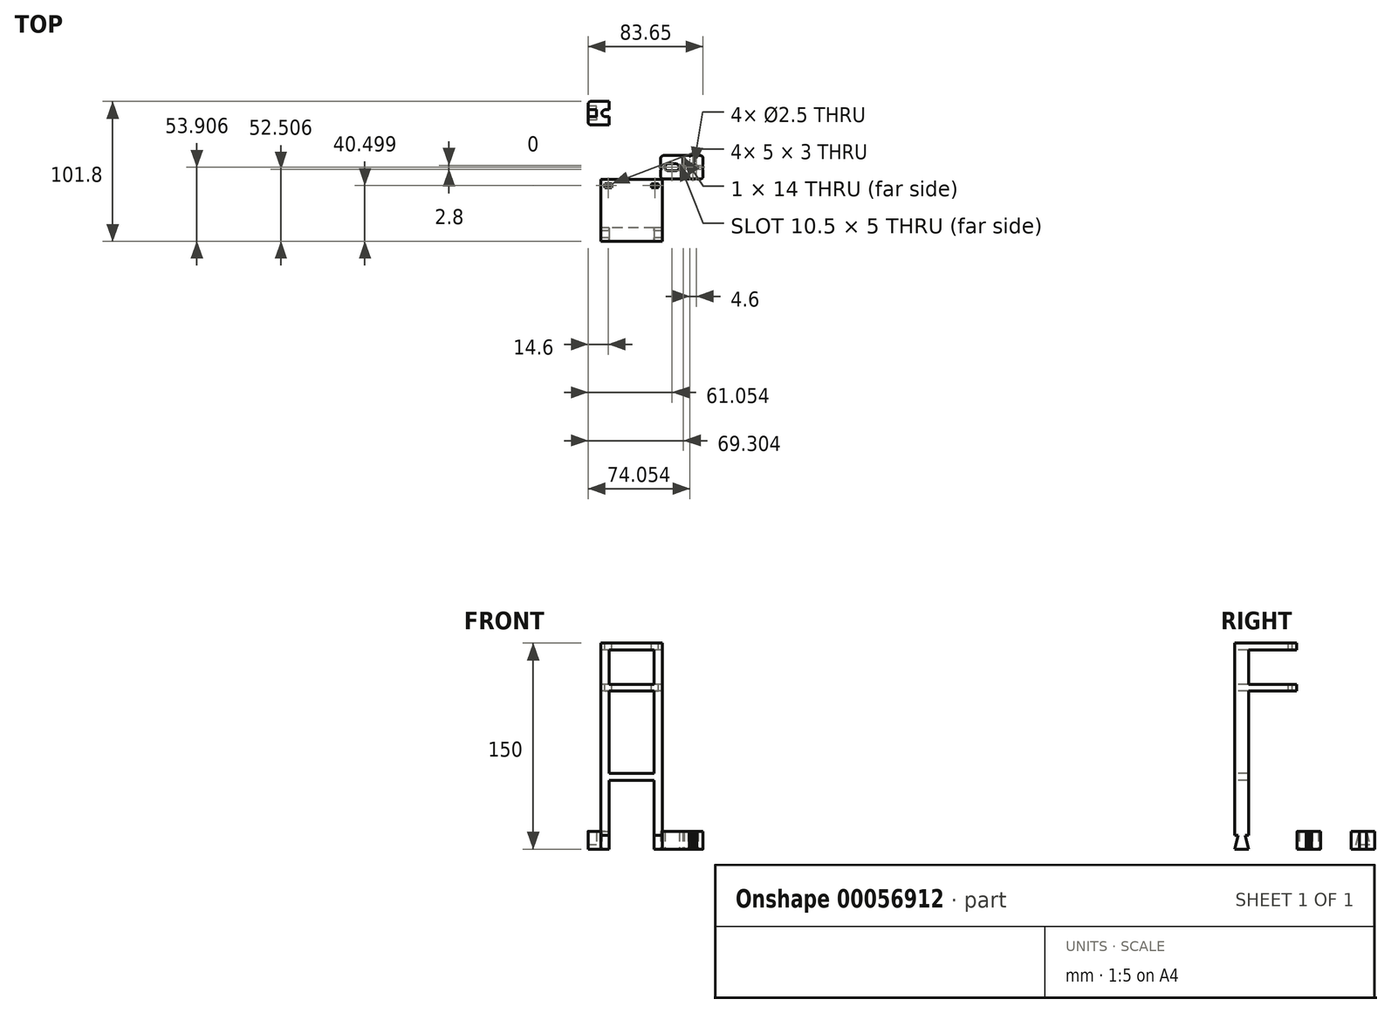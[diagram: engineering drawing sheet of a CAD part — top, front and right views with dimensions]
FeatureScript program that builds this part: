
annotation { "Feature Type Name" : "Feature", "Feature Type Description" : "" }
export const myFeature = defineFeature(function(context is Context, id is Id, definition is map)
    precondition{}
    {
        {
            var Q0;
            Q0=qCreatedBy(makeId("Top.planeOp"),FACE);
            var sketch = newSketch(context, id + "F0", { "sketchPlane" : qUnion([Q0])});
            skLineSegment(sketch, "E0.bottom", {"start": v(1.1, 9.76) * mm, "end": v(19.85, 9.76) * mm});
            skLineSegment(sketch, "E0.top", {"start": v(1.1, -7.24) * mm, "end": v(19.85, -7.24) * mm});
            skLineSegment(sketch, "E0.left", {"start": v(-0.9, 7.76) * mm, "end": v(-0.9, 3.16) * mm});
            skLineSegment(sketch, "E0.right", {"start": v(29.95, 7.76) * mm, "end": v(29.95, 3.16) * mm});
            skCircle(sketch, "E1", {"center": v(20.35, 1.26) * mm, "radius": 1.25 * mm});
            skCircle(sketch, "E2", {"center": v(24.95, 1.26) * mm, "radius": 1.25 * mm});
            skCircle(sketch, "E3", {"center": v(22.65, 2.66) * mm, "radius": 1.25 * mm});
            skCircle(sketch, "E4", {"center": v(22.65, -0.14) * mm, "radius": 1.25 * mm});
            skPoint(sketch, "E5.visualSharp", {"position": v(29.95, 9.76) * mm});
            skArc(sketch, "E5.filletArc", {"start": v(29.95, 7.76) * mm, "mid": v(29.37, 9.17) * mm, "end": v(27.95, 9.76) * mm});
            skPoint(sketch, "E6.visualSharp", {"position": v(29.95, -7.24) * mm});
            skArc(sketch, "E6.filletArc", {"start": v(27.95, -7.24) * mm, "mid": v(29.37, -6.66) * mm, "end": v(29.95, -5.24) * mm});
            skLineSegment(sketch, "E7.bottom", {"start": v(15.1, 8.26) * mm, "end": v(16.1, 8.26) * mm});
            skLineSegment(sketch, "E7.top", {"start": v(15.1, -5.74) * mm, "end": v(16.1, -5.74) * mm});
            skLineSegment(sketch, "E7.left", {"start": v(15.1, 8.26) * mm, "end": v(15.1, -5.74) * mm});
            skLineSegment(sketch, "E7.right", {"start": v(16.1, 8.26) * mm, "end": v(16.1, -5.74) * mm});
            skArc(sketch, "E8", {"start": v(10.1, -1.24) * mm, "mid": v(12.6, 1.26) * mm, "end": v(10.1, 3.76) * mm});
            skPoint(sketch, "E8.centerSnap0", {"position": v(15.1, 1.26) * mm});
            skArc(sketch, "E9", {"start": v(4.6, 3.76) * mm, "mid": v(2.1, 1.26) * mm, "end": v(4.6, -1.24) * mm});
            skLineSegment(sketch, "E10", {"start": v(4.6, 3.76) * mm, "end": v(10.1, 3.76) * mm});
            skLineSegment(sketch, "E11", {"start": v(4.6, -1.24) * mm, "end": v(10.1, -1.24) * mm});
            skPoint(sketch, "E12.visualSharp", {"position": v(-0.9, 9.76) * mm});
            skArc(sketch, "E12.filletArc", {"start": v(1.1, 9.76) * mm, "mid": v(-0.31, 9.17) * mm, "end": v(-0.9, 7.76) * mm});
            skPoint(sketch, "E13.visualSharp", {"position": v(-0.9, -7.24) * mm});
            skArc(sketch, "E13.filletArc", {"start": v(-0.9, -5.24) * mm, "mid": v(-0.31, -6.66) * mm, "end": v(1.1, -7.24) * mm});
            skArc(sketch, "E14", {"start": v(19.85, 9.76) * mm, "mid": v(20.35, 9.26) * mm, "end": v(20.85, 9.76) * mm});
            skArc(sketch, "E15", {"start": v(22.15, 9.76) * mm, "mid": v(22.65, 9.26) * mm, "end": v(23.15, 9.76) * mm});
            skArc(sketch, "E16", {"start": v(24.45, 9.76) * mm, "mid": v(24.95, 9.26) * mm, "end": v(25.45, 9.76) * mm});
            skArc(sketch, "E17", {"start": v(20.85, -7.24) * mm, "mid": v(20.35, -6.74) * mm, "end": v(19.85, -7.24) * mm});
            skArc(sketch, "E18", {"start": v(23.15, -7.24) * mm, "mid": v(22.65, -6.74) * mm, "end": v(22.15, -7.24) * mm});
            skArc(sketch, "E19", {"start": v(25.45, -7.24) * mm, "mid": v(24.95, -6.74) * mm, "end": v(24.45, -7.24) * mm});
            skArc(sketch, "E20", {"start": v(29.95, 3.16) * mm, "mid": v(29.45, 2.66) * mm, "end": v(29.95, 2.16) * mm});
            skArc(sketch, "E21", {"start": v(29.95, 1.76) * mm, "mid": v(29.45, 1.26) * mm, "end": v(29.95, 0.76) * mm});
            skArc(sketch, "E22", {"start": v(29.95, 0.36) * mm, "mid": v(29.45, -0.14) * mm, "end": v(29.95, -0.64) * mm});
            skArc(sketch, "E23", {"start": v(-0.9, 2.16) * mm, "mid": v(-0.4, 2.66) * mm, "end": v(-0.9, 3.16) * mm});
            skArc(sketch, "E24", {"start": v(-0.9, 0.76) * mm, "mid": v(-0.4, 1.26) * mm, "end": v(-0.9, 1.76) * mm});
            skArc(sketch, "E25", {"start": v(-0.9, -0.64) * mm, "mid": v(-0.4, -0.14) * mm, "end": v(-0.9, 0.36) * mm});
            skLineSegment(sketch, "E26.trimOffspring", {"start": v(20.85, 9.76) * mm, "end": v(22.15, 9.76) * mm});
            skLineSegment(sketch, "E27.trimOffspring", {"start": v(23.15, 9.76) * mm, "end": v(24.45, 9.76) * mm});
            skLineSegment(sketch, "E28.trimOffspring", {"start": v(25.45, 9.76) * mm, "end": v(27.95, 9.76) * mm});
            skLineSegment(sketch, "E29.trimOffspring", {"start": v(29.95, 2.16) * mm, "end": v(29.95, 1.76) * mm});
            skLineSegment(sketch, "E30.trimOffspring", {"start": v(29.95, 0.76) * mm, "end": v(29.95, 0.36) * mm});
            skLineSegment(sketch, "E31.trimOffspring", {"start": v(29.95, -0.64) * mm, "end": v(29.95, -5.24) * mm});
            skLineSegment(sketch, "E32.trimOffspring", {"start": v(25.45, -7.24) * mm, "end": v(27.95, -7.24) * mm});
            skLineSegment(sketch, "E33.trimOffspring", {"start": v(23.15, -7.24) * mm, "end": v(24.45, -7.24) * mm});
            skLineSegment(sketch, "E34.trimOffspring", {"start": v(20.85, -7.24) * mm, "end": v(22.15, -7.24) * mm});
            skLineSegment(sketch, "E35.trimOffspring", {"start": v(-0.9, -0.64) * mm, "end": v(-0.9, -5.24) * mm});
            skLineSegment(sketch, "E36.trimOffspring", {"start": v(-0.9, 0.76) * mm, "end": v(-0.9, 0.36) * mm});
            skLineSegment(sketch, "E37.trimOffspring", {"start": v(-0.9, 2.16) * mm, "end": v(-0.9, 1.76) * mm});
            skSolve(sketch);
        }
        {
            var Q0;
            Q0 = qSketchRegion(id + "F0", true);
            extrude(context, id + "F1", {"entities" : qUnion([Q0]), "depth" : 13 * mm});
        }
        {
            var Q0;
            Q0=qCreatedBy(makeId("Top.planeOp"),FACE);
            var sketch = newSketch(context, id + "F2", { "sketchPlane" : qUnion([Q0])});
            skPoint(sketch, "E38.visualSharp", {"position": v(-53.7, 49.15) * mm});
            skLineSegment(sketch, "E39", {"start": v(-41.2, 43.15) * mm, "end": v(-35.7, 43.15) * mm});
            skLineSegment(sketch, "E40.left", {"start": v(-30.7, 47.65) * mm, "end": v(-30.7, 33.65) * mm});
            skCircle(sketch, "E41", {"center": v(-20.85, 40.65) * mm, "radius": 1.25 * mm});
            skPoint(sketch, "E42.visualSharp", {"position": v(-8.85, 49.15) * mm});
            skLineSegment(sketch, "E43", {"start": v(-41.2, 38.15) * mm, "end": v(-35.7, 38.15) * mm});
            skPoint(sketch, "E44.visualSharp", {"position": v(-53.7, 32.15) * mm});
            skLineSegment(sketch, "E45.top", {"start": v(-51.7, 32.15) * mm, "end": v(-25.95, 32.15) * mm});
            skLineSegment(sketch, "E45.bottom", {"start": v(-51.7, 49.15) * mm, "end": v(-25.95, 49.15) * mm});
            skArc(sketch, "E46", {"start": v(-41.2, 43.15) * mm, "mid": v(-43.7, 40.65) * mm, "end": v(-41.2, 38.15) * mm});
            skPoint(sketch, "E47.visualSharp", {"position": v(-8.85, 32.15) * mm});
            skArc(sketch, "E48", {"start": v(-35.7, 38.15) * mm, "mid": v(-33.2, 40.65) * mm, "end": v(-35.7, 43.15) * mm});
            skLineSegment(sketch, "E40.right", {"start": v(-29.7, 47.65) * mm, "end": v(-29.7, 33.65) * mm});
            skPoint(sketch, "E48.centerSnap0", {"position": v(-30.7, 40.65) * mm});
            skCircle(sketch, "E49", {"center": v(-25.45, 40.65) * mm, "radius": 1.25 * mm});
            skCircle(sketch, "E50", {"center": v(-23.15, 42.05) * mm, "radius": 1.25 * mm});
            skCircle(sketch, "E51", {"center": v(-23.15, 39.25) * mm, "radius": 1.25 * mm});
            skLineSegment(sketch, "E52.trimOffspring", {"start": v(-20.35, 32.15) * mm, "end": v(-10.85, 32.15) * mm});
            skArc(sketch, "E42.filletArc", {"start": v(-8.85, 47.15) * mm, "mid": v(-9.43, 48.56) * mm, "end": v(-10.85, 49.15) * mm});
            skArc(sketch, "E47.filletArc", {"start": v(-10.85, 32.15) * mm, "mid": v(-9.43, 32.73) * mm, "end": v(-8.85, 34.15) * mm});
            skLineSegment(sketch, "E40.bottom", {"start": v(-30.7, 47.65) * mm, "end": v(-29.7, 47.65) * mm});
            skLineSegment(sketch, "E40.top", {"start": v(-30.7, 33.65) * mm, "end": v(-29.7, 33.65) * mm});
            skArc(sketch, "E44.filletArc", {"start": v(-53.7, 34.15) * mm, "mid": v(-53.1, 32.73) * mm, "end": v(-51.7, 32.15) * mm});
            skArc(sketch, "E38.filletArc", {"start": v(-51.7, 49.15) * mm, "mid": v(-53.1, 48.56) * mm, "end": v(-53.7, 47.15) * mm});
            skLineSegment(sketch, "E53.trimOffspring", {"start": v(-20.35, 49.15) * mm, "end": v(-10.85, 49.15) * mm});
            skLineSegment(sketch, "E54.trimOffspring", {"start": v(-22.65, 32.15) * mm, "end": v(-21.35, 32.15) * mm});
            skArc(sketch, "E55", {"start": v(-24.95, 32.15) * mm, "mid": v(-25.45, 32.65) * mm, "end": v(-25.95, 32.15) * mm});
            skArc(sketch, "E56", {"start": v(-25.95, 49.15) * mm, "mid": v(-25.45, 48.65) * mm, "end": v(-24.95, 49.15) * mm});
            skLineSegment(sketch, "E57.trimOffspring", {"start": v(-24.95, 49.15) * mm, "end": v(-23.65, 49.15) * mm});
            skLineSegment(sketch, "E58.trimOffspring", {"start": v(-24.95, 32.15) * mm, "end": v(-23.65, 32.15) * mm});
            skArc(sketch, "E59", {"start": v(-22.65, 32.15) * mm, "mid": v(-23.15, 32.65) * mm, "end": v(-23.65, 32.15) * mm});
            skArc(sketch, "E60", {"start": v(-20.35, 32.15) * mm, "mid": v(-20.85, 32.65) * mm, "end": v(-21.35, 32.15) * mm});
            skArc(sketch, "E61", {"start": v(-21.35, 49.15) * mm, "mid": v(-20.85, 48.65) * mm, "end": v(-20.35, 49.15) * mm});
            skLineSegment(sketch, "E62.trimOffspring", {"start": v(-22.65, 49.15) * mm, "end": v(-21.35, 49.15) * mm});
            skArc(sketch, "E63", {"start": v(-23.65, 49.15) * mm, "mid": v(-23.15, 48.65) * mm, "end": v(-22.65, 49.15) * mm});
            skLineSegment(sketch, "E64", {"start": v(-8.85, 34.15) * mm, "end": v(-8.85, 47.15) * mm});
            skLineSegment(sketch, "E65", {"start": v(-53.7, 34.15) * mm, "end": v(-53.7, 47.15) * mm});
            skSolve(sketch);
        }
        {
            var Q0;
            Q0 = qSketchRegion(id + "F2", true);
            extrude(context, id + "F3", {"entities" : qUnion([Q0]), "depth" : 13 * mm});
        }
        {
            var Q0;
            Q0=makeQuery(id+"F3.opExtrude","SWEPT_FACE",FACE,{"disambiguationData":[OSD([sQuery(id+"F2.wireOp",EDGE,"E64")])]});
            var sketch = newSketch(context, id + "F4", { "sketchPlane" : qUnion([Q0])});
            skLineSegment(sketch, "E66", {"start": v(38.15, 13) * mm, "end": v(35.65, 3) * mm});
            skLineSegment(sketch, "E67", {"start": v(35.65, 3) * mm, "end": v(45.64, 3) * mm});
            skLineSegment(sketch, "E68", {"start": v(45.64, 3) * mm, "end": v(43.15, 13) * mm});
            skLineSegment(sketch, "E69", {"start": v(43.15, 13) * mm, "end": v(38.15, 13) * mm});
            skSolve(sketch);
        }
        {
            var Q0;
            Q0 = qSketchRegion(id + "F4", true);
            extrude(context, id + "F5", {"entities" : qUnion([Q0]), "operationType" : NewBodyOperationType.REMOVE, "oppositeDirection" : true, "depth" : 6 * mm});
        }
        {
            var Q0;
            Q0=makeQuery(id+"F3.opExtrude","SWEPT_FACE",FACE,{"disambiguationData":[OSD([sQuery(id+"F2.wireOp",EDGE,"E65")])]});
            var sketch = newSketch(context, id + "F6", { "sketchPlane" : qUnion([Q0])});
            skLineSegment(sketch, "E70", {"start": v(-43.15, 13) * mm, "end": v(-45.64, 3) * mm});
            skLineSegment(sketch, "E71", {"start": v(-45.64, 3) * mm, "end": v(-35.65, 3) * mm});
            skLineSegment(sketch, "E72", {"start": v(-35.65, 3) * mm, "end": v(-38.15, 13) * mm});
            skLineSegment(sketch, "E73", {"start": v(-38.15, 13) * mm, "end": v(-43.15, 13) * mm});
            skSolve(sketch);
        }
        {
            var Q0;
            Q0 = qSketchRegion(id + "F6", true);
            extrude(context, id + "F7", {"entities" : qUnion([Q0]), "operationType" : NewBodyOperationType.REMOVE, "oppositeDirection" : true, "depth" : 6 * mm});
        }
        {
            var Q0;
            Q0=qCreatedBy(makeId("Top.planeOp"),FACE);
            var sketch = newSketch(context, id + "F8", { "sketchPlane" : qUnion([Q0])});
            skLineSegment(sketch, "E74.bottom", {"start": v(-44.6, -42.65) * mm, "end": v(0.4, -42.65) * mm});
            skLineSegment(sketch, "E74.top", {"start": v(-44.6, -52.65) * mm, "end": v(0.4, -52.65) * mm});
            skLineSegment(sketch, "E74.left", {"start": v(-44.6, -42.65) * mm, "end": v(-44.6, -52.65) * mm});
            skLineSegment(sketch, "E74.right", {"start": v(0.4, -42.65) * mm, "end": v(0.4, -52.65) * mm});
            skSolve(sketch);
        }
        {
            var Q0;
            Q0 = qSketchRegion(id + "F8", true);
            extrude(context, id + "F9", {"entities" : qUnion([Q0]), "depth" : 150 * mm});
        }
        {
            var Q0;
            Q0=makeQuery(id+"F9.opExtrude","SWEPT_FACE",FACE,{"disambiguationData":[OSD([sQuery(id+"F8.wireOp",EDGE,"E74.left")])]});
            var sketch = newSketch(context, id + "F10", { "sketchPlane" : qUnion([Q0])});
            skLineSegment(sketch, "E75", {"start": v(42.66, 0) * mm, "end": v(45.15, 10) * mm});
            skLineSegment(sketch, "E76", {"start": v(45.15, 10) * mm, "end": v(42.65, 10) * mm});
            skLineSegment(sketch, "E77", {"start": v(42.65, 10) * mm, "end": v(42.65, 0) * mm});
            skLineSegment(sketch, "E78", {"start": v(42.65, 0) * mm, "end": v(42.66, 0) * mm});
            skLineSegment(sketch, "E79", {"start": v(52.64, 0) * mm, "end": v(50.15, 10) * mm});
            skLineSegment(sketch, "E80", {"start": v(50.15, 10) * mm, "end": v(52.65, 10) * mm});
            skLineSegment(sketch, "E81", {"start": v(52.65, 10) * mm, "end": v(52.65, 0) * mm});
            skLineSegment(sketch, "E82", {"start": v(52.65, 0) * mm, "end": v(52.64, 0) * mm});
            skSolve(sketch);
        }
        {
            var Q0;
            Q0 = qSketchRegion(id + "F10", true);
            extrude(context, id + "F11", {"entities" : qUnion([Q0]), "operationType" : NewBodyOperationType.REMOVE, "endBound" : BoundingType.THROUGH_ALL, "oppositeDirection" : true, "depth" : 25 * mm});
        }
        {
            var Q0;
            Q0=makeQuery(id+"F9.opExtrude","SWEPT_FACE",FACE,{"disambiguationData":[OSD([sQuery(id+"F8.wireOp",EDGE,"E74.top")])]});
            var sketch = newSketch(context, id + "F12", { "sketchPlane" : qUnion([Q0])});
            skLineSegment(sketch, "E83.bottom", {"start": v(-38.6, 50) * mm, "end": v(-5.6, 50) * mm});
            skLineSegment(sketch, "E83.top", {"start": v(-38.6, 0) * mm, "end": v(-5.6, 0) * mm});
            skLineSegment(sketch, "E83.left", {"start": v(-38.6, 50) * mm, "end": v(-38.6, 0) * mm});
            skLineSegment(sketch, "E83.right", {"start": v(-5.6, 50) * mm, "end": v(-5.6, 0) * mm});
            skLineSegment(sketch, "E84.bottom", {"start": v(-38.6, 55) * mm, "end": v(-5.6, 55) * mm});
            skLineSegment(sketch, "E84.top", {"start": v(-38.6, 115) * mm, "end": v(-5.6, 115) * mm});
            skLineSegment(sketch, "E84.left", {"start": v(-38.6, 55) * mm, "end": v(-38.6, 115) * mm});
            skLineSegment(sketch, "E84.right", {"start": v(-5.6, 55) * mm, "end": v(-5.6, 115) * mm});
            skLineSegment(sketch, "E85.bottom", {"start": v(-38.6, 120) * mm, "end": v(-5.6, 120) * mm});
            skLineSegment(sketch, "E85.top", {"start": v(-38.6, 145) * mm, "end": v(-5.6, 145) * mm});
            skLineSegment(sketch, "E85.left", {"start": v(-38.6, 120) * mm, "end": v(-38.6, 145) * mm});
            skLineSegment(sketch, "E85.right", {"start": v(-5.6, 120) * mm, "end": v(-5.6, 145) * mm});
            skSolve(sketch);
        }
        {
            var Q0;
            Q0 = qSketchRegion(id + "F12", true);
            extrude(context, id + "F13", {"entities" : qUnion([Q0]), "operationType" : NewBodyOperationType.REMOVE, "endBound" : BoundingType.THROUGH_ALL, "oppositeDirection" : true, "depth" : 25 * mm});
        }
        {
            var Q0;
            Q0=makeQuery(id+"F9.opExtrude","SWEPT_FACE",FACE,{"disambiguationData":[OSD([sQuery(id+"F8.wireOp",EDGE,"E74.bottom")])]});
            var sketch = newSketch(context, id + "F14", { "sketchPlane" : qUnion([Q0])});
            skLineSegment(sketch, "E86.bottom", {"start": v(-0.4, 150) * mm, "end": v(44.6, 150) * mm});
            skLineSegment(sketch, "E86.top", {"start": v(-0.4, 145) * mm, "end": v(44.6, 145) * mm});
            skLineSegment(sketch, "E86.left", {"start": v(-0.4, 150) * mm, "end": v(-0.4, 145) * mm});
            skLineSegment(sketch, "E86.right", {"start": v(44.6, 150) * mm, "end": v(44.6, 145) * mm});
            skLineSegment(sketch, "E87.bottom", {"start": v(-0.4, 120) * mm, "end": v(44.6, 120) * mm});
            skLineSegment(sketch, "E87.top", {"start": v(-0.4, 115) * mm, "end": v(44.6, 115) * mm});
            skLineSegment(sketch, "E87.left", {"start": v(-0.4, 120) * mm, "end": v(-0.4, 115) * mm});
            skLineSegment(sketch, "E87.right", {"start": v(44.6, 120) * mm, "end": v(44.6, 115) * mm});
            skSolve(sketch);
        }
        {
            var Q0;
            Q0 = qSketchRegion(id + "F14", true);
            extrude(context, id + "F15", {"entities" : qUnion([Q0]), "operationType" : NewBodyOperationType.ADD, "depth" : 35 * mm});
        }
        {
            var Q0;
            Q0=makeQuery(id+"F15.boolean.opBoolean","MERGE",FACE,{"derivedFrom":[makeQuery(id+"F9.opExtrude","CAP_FACE",FACE,{"disambiguationData":[OSD([sQuery(id+"F8.wireOp",EDGE,"E74.bottom"),sQuery(id+"F8.wireOp",EDGE,"E74.top"),sQuery(id+"F8.wireOp",EDGE,"E74.left"),sQuery(id+"F8.wireOp",EDGE,"E74.right")])],"isStart":false}),makeQuery(id+"F15.opExtrude","SWEPT_FACE",FACE,{"disambiguationData":[OSD([sQuery(id+"F14.wireOp",EDGE,"E86.bottom")])]})]});
            var sketch = newSketch(context, id + "F16", { "sketchPlane" : qUnion([Q0])});
            skLineSegment(sketch, "E88.bottom", {"start": v(-41.6, -10.65) * mm, "end": v(-36.6, -10.65) * mm});
            skLineSegment(sketch, "E88.top", {"start": v(-41.6, -13.65) * mm, "end": v(-36.6, -13.65) * mm});
            skLineSegment(sketch, "E88.left", {"start": v(-41.6, -10.65) * mm, "end": v(-41.6, -13.65) * mm});
            skLineSegment(sketch, "E88.right", {"start": v(-36.6, -10.65) * mm, "end": v(-36.6, -13.65) * mm});
            skLineSegment(sketch, "E89.bottom", {"start": v(-7.6, -10.65) * mm, "end": v(-2.6, -10.65) * mm});
            skLineSegment(sketch, "E89.top", {"start": v(-7.6, -13.65) * mm, "end": v(-2.6, -13.65) * mm});
            skLineSegment(sketch, "E89.left", {"start": v(-7.6, -10.65) * mm, "end": v(-7.6, -13.65) * mm});
            skLineSegment(sketch, "E89.right", {"start": v(-2.6, -10.65) * mm, "end": v(-2.6, -13.65) * mm});
            skSolve(sketch);
        }
        {
            var Q0;
            Q0 = qSketchRegion(id + "F16", true);
            var Q1;
            Q1=makeQuery(id+"F15.boolean.opBoolean","MERGE",FACE,{"derivedFrom":[makeQuery(id+"F13.boolean.opBoolean","COPY",FACE,{"derivedFrom":makeQuery(id+"F13.opExtrude","SWEPT_FACE",FACE,{"disambiguationData":[OSD([sQuery(id+"F12.wireOp",EDGE,"E84.top")])]})}),makeQuery(id+"F15.opExtrude","SWEPT_FACE",FACE,{"disambiguationData":[OSD([sQuery(id+"F14.wireOp",EDGE,"E87.top")])]})]});
            extrude(context, id + "F17", {"entities" : qUnion([Q0]), "operationType" : NewBodyOperationType.REMOVE, "endBound" : BoundingType.UP_TO_SURFACE, "oppositeDirection" : true, "endBoundEntityFace" : qUnion([Q1]), "depth" : 25 * mm});
        }
    });
